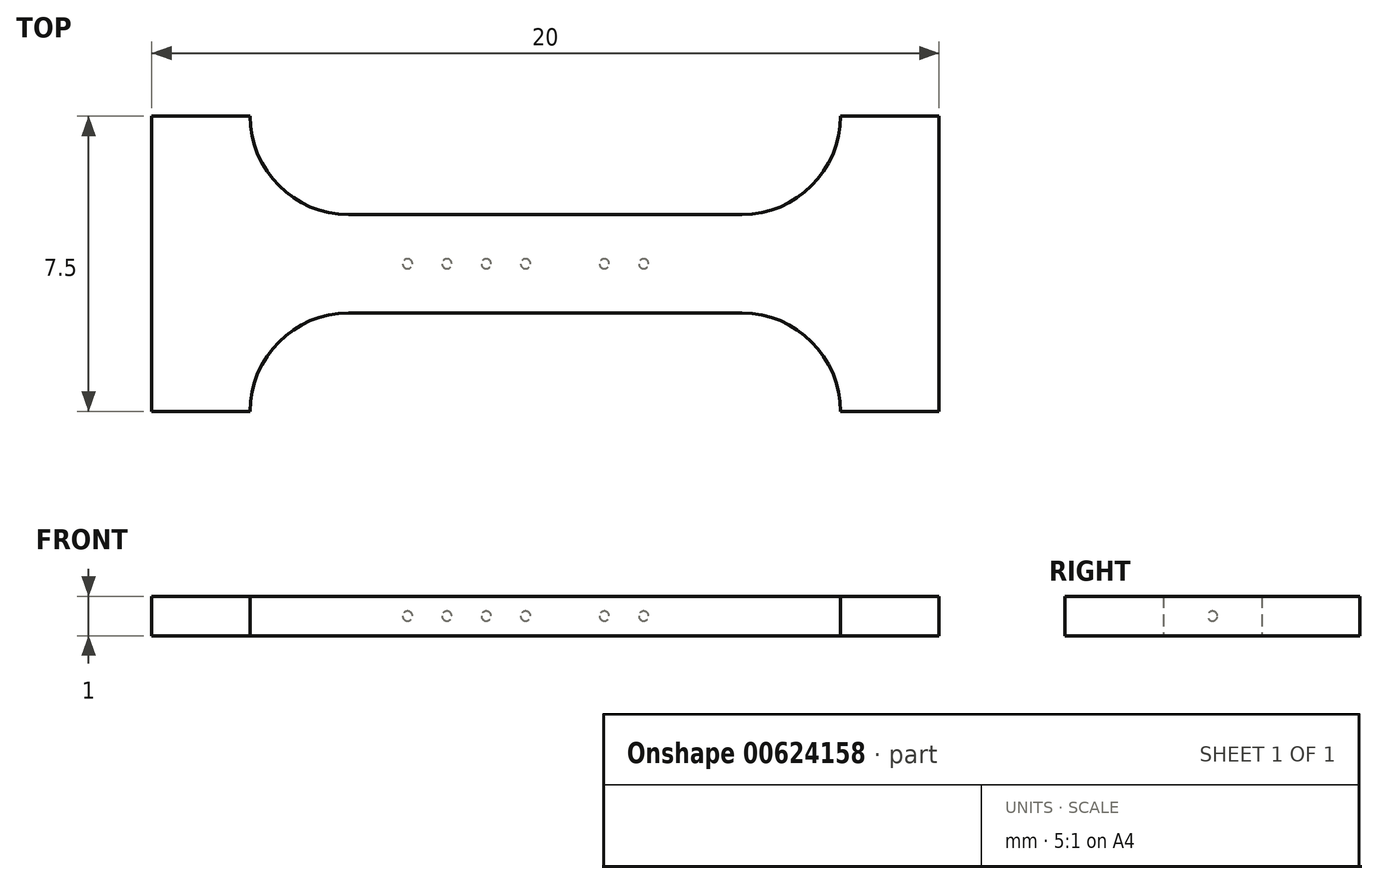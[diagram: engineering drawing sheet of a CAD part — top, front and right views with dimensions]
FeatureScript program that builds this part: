
annotation { "Feature Type Name" : "Feature", "Feature Type Description" : "" }
export const myFeature = defineFeature(function(context is Context, id is Id, definition is map)
    precondition{}
    {
        {
            var Q0;
            Q0=qCreatedBy(makeId("Top.planeOp"),FACE);
            var sketch = newSketch(context, id + "F0", { "sketchPlane" : qUnion([Q0])});
            skLineSegment(sketch, "E0.bottom", {"start": v(5, -1.25) * mm, "end": v(-5, -1.25) * mm, "construction": true});
            skLineSegment(sketch, "E0.top", {"start": v(5, 1.25) * mm, "end": v(-5, 1.25) * mm, "construction": true});
            skLineSegment(sketch, "E0.left", {"start": v(5, -1.25) * mm, "end": v(5, 1.25) * mm, "construction": true});
            skLineSegment(sketch, "E0.right", {"start": v(-5, -1.25) * mm, "end": v(-5, 1.25) * mm, "construction": true});
            skPoint(sketch, "E0.middle", {"position": v(0, 0) * mm});
            skLineSegment(sketch, "E1.bottom", {"start": v(5, 1.25) * mm, "end": v(7.5, 1.25) * mm, "construction": true});
            skLineSegment(sketch, "E1.top", {"start": v(5, -1.25) * mm, "end": v(7.5, -1.25) * mm, "construction": true});
            skLineSegment(sketch, "E1.left", {"start": v(5, 1.25) * mm, "end": v(5, -1.25) * mm, "construction": true});
            skLineSegment(sketch, "E1.right", {"start": v(7.5, 1.25) * mm, "end": v(7.5, -1.25) * mm, "construction": true});
            skLineSegment(sketch, "E2.bottom", {"start": v(7.5, 1.25) * mm, "end": v(10, 1.25) * mm, "construction": true});
            skLineSegment(sketch, "E2.top", {"start": v(7.5, -1.25) * mm, "end": v(10, -1.25) * mm, "construction": true});
            skLineSegment(sketch, "E2.right", {"start": v(10, 1.25) * mm, "end": v(10, -1.25) * mm, "construction": true});
            skLineSegment(sketch, "E3.top", {"start": v(7.5, 3.75) * mm, "end": v(10, 3.75) * mm, "construction": true});
            skLineSegment(sketch, "E3.left", {"start": v(7.5, 1.25) * mm, "end": v(7.5, 3.75) * mm, "construction": true});
            skLineSegment(sketch, "E3.right", {"start": v(10, 1.25) * mm, "end": v(10, 3.75) * mm, "construction": true});
            skLineSegment(sketch, "E4.top", {"start": v(7.5, -3.75) * mm, "end": v(10, -3.75) * mm, "construction": true});
            skLineSegment(sketch, "E4.left", {"start": v(7.5, -1.25) * mm, "end": v(7.5, -3.75) * mm, "construction": true});
            skLineSegment(sketch, "E4.right", {"start": v(10, -1.25) * mm, "end": v(10, -3.75) * mm, "construction": true});
            skLineSegment(sketch, "E5.bottom", {"start": v(7.5, 1.25) * mm, "end": v(5, 1.25) * mm, "construction": true});
            skLineSegment(sketch, "E5.top", {"start": v(7.5, 3.75) * mm, "end": v(5, 3.75) * mm, "construction": true});
            skLineSegment(sketch, "E5.right", {"start": v(5, 1.25) * mm, "end": v(5, 3.75) * mm, "construction": true});
            skArc(sketch, "E6", {"start": v(5, 1.25) * mm, "mid": v(6.77, 1.98) * mm, "end": v(7.5, 3.75) * mm});
            skLineSegment(sketch, "E7.top", {"start": v(5, -3.75) * mm, "end": v(7.5, -3.75) * mm, "construction": true});
            skLineSegment(sketch, "E7.left", {"start": v(5, -1.25) * mm, "end": v(5, -3.75) * mm, "construction": true});
            skArc(sketch, "E8", {"start": v(5, -1.25) * mm, "mid": v(6.77, -1.98) * mm, "end": v(7.5, -3.75) * mm});
            skLineSegment(sketch, "E9", {"start": v(7.5, -3.75) * mm, "end": v(10, -3.75) * mm});
            skLineSegment(sketch, "E10", {"start": v(10, -3.75) * mm, "end": v(10, 3.75) * mm});
            skLineSegment(sketch, "E11", {"start": v(10, 3.75) * mm, "end": v(7.5, 3.75) * mm});
            skLineSegment(sketch, "E12", {"start": v(0, 1.25) * mm, "end": v(0, -1.25) * mm, "construction": true});
            skLineSegment(sketch, "E13", {"start": v(5, 1.25) * mm, "end": v(0, 1.25) * mm});
            skLineSegment(sketch, "E14", {"start": v(0, 1.25) * mm, "end": v(0, -1.25) * mm});
            skLineSegment(sketch, "E15", {"start": v(0, -1.25) * mm, "end": v(5, -1.25) * mm});
            skLineSegment(sketch, "E16.bottom", {"start": v(-5, 1.25) * mm, "end": v(-7.5, 1.25) * mm, "construction": true});
            skLineSegment(sketch, "E16.top", {"start": v(-5, -1.25) * mm, "end": v(-7.5, -1.25) * mm, "construction": true});
            skLineSegment(sketch, "E16.left", {"start": v(-5, 1.25) * mm, "end": v(-5, -1.25) * mm, "construction": true});
            skLineSegment(sketch, "E16.right", {"start": v(-7.5, 1.25) * mm, "end": v(-7.5, -1.25) * mm, "construction": true});
            skLineSegment(sketch, "E17.bottom", {"start": v(-7.5, 1.25) * mm, "end": v(-10, 1.25) * mm, "construction": true});
            skLineSegment(sketch, "E17.top", {"start": v(-7.5, -1.25) * mm, "end": v(-10, -1.25) * mm, "construction": true});
            skLineSegment(sketch, "E17.right", {"start": v(-10, 1.25) * mm, "end": v(-10, -1.25) * mm, "construction": true});
            skLineSegment(sketch, "E18.bottom", {"start": v(-10, 1.25) * mm, "end": v(-7.5, 1.25) * mm, "construction": true});
            skLineSegment(sketch, "E18.top", {"start": v(-10, 3.75) * mm, "end": v(-7.5, 3.75) * mm, "construction": true});
            skLineSegment(sketch, "E18.left", {"start": v(-10, 1.25) * mm, "end": v(-10, 3.75) * mm, "construction": true});
            skLineSegment(sketch, "E18.right", {"start": v(-7.5, 1.25) * mm, "end": v(-7.5, 3.75) * mm, "construction": true});
            skLineSegment(sketch, "E19.bottom", {"start": v(-7.5, 3.75) * mm, "end": v(-5, 3.75) * mm, "construction": true});
            skLineSegment(sketch, "E19.top", {"start": v(-7.5, 1.25) * mm, "end": v(-5, 1.25) * mm, "construction": true});
            skLineSegment(sketch, "E19.left", {"start": v(-7.5, 3.75) * mm, "end": v(-7.5, 1.25) * mm, "construction": true});
            skLineSegment(sketch, "E19.right", {"start": v(-5, 3.75) * mm, "end": v(-5, 1.25) * mm, "construction": true});
            skLineSegment(sketch, "E20.bottom", {"start": v(-7.5, -1.25) * mm, "end": v(-5, -1.25) * mm, "construction": true});
            skLineSegment(sketch, "E20.top", {"start": v(-7.5, -3.75) * mm, "end": v(-5, -3.75) * mm, "construction": true});
            skLineSegment(sketch, "E20.left", {"start": v(-7.5, -1.25) * mm, "end": v(-7.5, -3.75) * mm, "construction": true});
            skLineSegment(sketch, "E20.right", {"start": v(-5, -1.25) * mm, "end": v(-5, -3.75) * mm, "construction": true});
            skLineSegment(sketch, "E21.bottom", {"start": v(-7.5, -3.75) * mm, "end": v(-10, -3.75) * mm, "construction": true});
            skLineSegment(sketch, "E21.left", {"start": v(-7.5, -3.75) * mm, "end": v(-7.5, -1.25) * mm, "construction": true});
            skLineSegment(sketch, "E21.right", {"start": v(-10, -3.75) * mm, "end": v(-10, -1.25) * mm, "construction": true});
            skArc(sketch, "E22", {"start": v(-7.5, 3.75) * mm, "mid": v(-6.77, 1.98) * mm, "end": v(-5, 1.25) * mm});
            skArc(sketch, "E23", {"start": v(-7.5, -3.75) * mm, "mid": v(-6.77, -1.98) * mm, "end": v(-5, -1.25) * mm});
            skLineSegment(sketch, "E24", {"start": v(-7.5, -3.75) * mm, "end": v(-10, -3.75) * mm});
            skLineSegment(sketch, "E25", {"start": v(-10, -3.75) * mm, "end": v(-10, 3.75) * mm});
            skLineSegment(sketch, "E26", {"start": v(-10, 3.75) * mm, "end": v(-7.5, 3.75) * mm});
            skLineSegment(sketch, "E27", {"start": v(-5, 1.25) * mm, "end": v(0, 1.25) * mm});
            skLineSegment(sketch, "E28", {"start": v(-5, -1.25) * mm, "end": v(0, -1.25) * mm});
            skSolve(sketch);
        }
        {
            var Q0;
            Q0=makeQuery(id+"F0.imprint","IMPRINT",FACE,{"disambiguationData":[TD([[makeQuery(id+"F0.imprint","IMPRINT",EDGE,{"derivedFrom":sQuery(id+"F0.wireOp",EDGE,"E14")}),-1.0]])]});
            var Q1;
            Q1=makeQuery(id+"F0.imprint","IMPRINT",FACE,{"disambiguationData":[TD([[makeQuery(id+"F0.imprint","IMPRINT",EDGE,{"derivedFrom":sQuery(id+"F0.wireOp",EDGE,"E6")}),-1.0]])]});
            extrude(context, id + "F1", {"entities" : qUnion([Q0, Q1]), "endBound" : BoundingType.SYMMETRIC, "depth" : 1 * mm, "offsetDistance" : 25 * mm});
        }
        {
            var Q0;
            Q0=qCreatedBy(makeId("Top.planeOp"),FACE);
            var sketch = newSketch(context, id + "F2", { "sketchPlane" : qUnion([Q0])});
            skLineSegment(sketch, "E29.bottom", {"start": v(5, -1.25) * mm, "end": v(-5, -1.25) * mm, "construction": true});
            skLineSegment(sketch, "E29.top", {"start": v(5, 1.25) * mm, "end": v(-5, 1.25) * mm, "construction": true});
            skLineSegment(sketch, "E29.left", {"start": v(5, -1.25) * mm, "end": v(5, 1.25) * mm, "construction": true});
            skLineSegment(sketch, "E29.right", {"start": v(-5, -1.25) * mm, "end": v(-5, 1.25) * mm, "construction": true});
            skPoint(sketch, "E29.middle", {"position": v(0, 0) * mm});
            skLineSegment(sketch, "E30.bottom", {"start": v(4.75, -1) * mm, "end": v(-4.75, -1) * mm, "construction": true});
            skLineSegment(sketch, "E30.top", {"start": v(4.75, 1) * mm, "end": v(-4.75, 1) * mm, "construction": true});
            skLineSegment(sketch, "E30.left", {"start": v(4.75, -1) * mm, "end": v(4.75, 1) * mm, "construction": true});
            skLineSegment(sketch, "E30.right", {"start": v(-4.75, -1) * mm, "end": v(-4.75, 1) * mm, "construction": true});
            skLineSegment(sketch, "E31", {"start": v(-4.75, 0) * mm, "end": v(4.75, 0) * mm});
            skCircle(sketch, "E32", {"center": v(-3.5, 0) * mm, "radius": 0.12 * mm});
            skCircle(sketch, "E33.1.0.0", {"center": v(-2.5, 0) * mm, "radius": 0.12 * mm});
            skCircle(sketch, "E33.2.0.0", {"center": v(-1.5, 0) * mm, "radius": 0.12 * mm});
            skCircle(sketch, "E33.3.0.0", {"center": v(-0.5, 0) * mm, "radius": 0.12 * mm});
            skCircle(sketch, "E33.4.0.0", {"center": v(0.5, 0) * mm, "radius": 0.12 * mm});
            skCircle(sketch, "E33.5.0.0", {"center": v(1.5, 0) * mm, "radius": 0.12 * mm});
            skCircle(sketch, "E33.6.0.0", {"center": v(2.5, 0) * mm, "radius": 0.12 * mm});
            skCircle(sketch, "E33.7.0.0", {"center": v(3.5, 0) * mm, "radius": 0.12 * mm});
            skLineSegment(sketch, "E33.direction1", {"start": v(-3.5, 0) * mm, "end": v(-2.5, 0) * mm, "construction": true});
            skSolve(sketch);
        }
        {
            var Q0;
            {var subQ0=sQuery(id+"F2.wireOp",EDGE,"E32");var subQ1=sQuery(id+"F2.wireOp",EDGE,"E31");var subQ2=makeQuery(id+"F2.imprint","INTERSECT",VERTEX,{"disambiguationData":[OD(0.0)],"derivedFrom":[subQ1,subQ0]});Q0=makeQuery(id+"F2.imprint","IMPRINT",FACE,{"disambiguationData":[TD([[makeQuery(id+"F2.imprint","IMPRINT",EDGE,{"disambiguationData":[TD([[subQ2,-1.0]])],"derivedFrom":subQ1}),-1.0]])]});}
            var Q1;
            {var subQ0=sQuery(id+"F2.wireOp",EDGE,"E33.1.0.0");var subQ1=sQuery(id+"F2.wireOp",EDGE,"E31");var subQ2=makeQuery(id+"F2.imprint","INTERSECT",VERTEX,{"disambiguationData":[OD(0.0)],"derivedFrom":[subQ1,subQ0]});Q1=makeQuery(id+"F2.imprint","IMPRINT",FACE,{"disambiguationData":[TD([[makeQuery(id+"F2.imprint","IMPRINT",EDGE,{"disambiguationData":[TD([[subQ2,-1.0]])],"derivedFrom":subQ1}),-1.0]])]});}
            var Q2;
            {var subQ0=sQuery(id+"F2.wireOp",EDGE,"E33.2.0.0");var subQ1=sQuery(id+"F2.wireOp",EDGE,"E31");var subQ2=makeQuery(id+"F2.imprint","INTERSECT",VERTEX,{"disambiguationData":[OD(0.0)],"derivedFrom":[subQ1,subQ0]});Q2=makeQuery(id+"F2.imprint","IMPRINT",FACE,{"disambiguationData":[TD([[makeQuery(id+"F2.imprint","IMPRINT",EDGE,{"disambiguationData":[TD([[subQ2,-1.0]])],"derivedFrom":subQ1}),-1.0]])]});}
            var Q3;
            {var subQ0=sQuery(id+"F2.wireOp",EDGE,"E33.3.0.0");var subQ1=sQuery(id+"F2.wireOp",EDGE,"E31");var subQ2=makeQuery(id+"F2.imprint","INTERSECT",VERTEX,{"disambiguationData":[OD(0.0)],"derivedFrom":[subQ1,subQ0]});Q3=makeQuery(id+"F2.imprint","IMPRINT",FACE,{"disambiguationData":[TD([[makeQuery(id+"F2.imprint","IMPRINT",EDGE,{"disambiguationData":[TD([[subQ2,-1.0]])],"derivedFrom":subQ1}),-1.0]])]});}
            var Q4;
            {var subQ0=sQuery(id+"F2.wireOp",EDGE,"E33.4.0.0");var subQ1=sQuery(id+"F2.wireOp",EDGE,"E31");var subQ2=makeQuery(id+"F2.imprint","INTERSECT",VERTEX,{"disambiguationData":[OD(0.0)],"derivedFrom":[subQ1,subQ0]});Q4=makeQuery(id+"F2.imprint","IMPRINT",FACE,{"disambiguationData":[TD([[makeQuery(id+"F2.imprint","IMPRINT",EDGE,{"disambiguationData":[TD([[subQ2,-1.0]])],"derivedFrom":subQ1}),-1.0]])]});}
            var Q5;
            {var subQ0=sQuery(id+"F2.wireOp",EDGE,"E33.5.0.0");var subQ1=sQuery(id+"F2.wireOp",EDGE,"E31");var subQ2=makeQuery(id+"F2.imprint","INTERSECT",VERTEX,{"disambiguationData":[OD(0.0)],"derivedFrom":[subQ1,subQ0]});Q5=makeQuery(id+"F2.imprint","IMPRINT",FACE,{"disambiguationData":[TD([[makeQuery(id+"F2.imprint","IMPRINT",EDGE,{"disambiguationData":[TD([[subQ2,-1.0]])],"derivedFrom":subQ1}),-1.0]])]});}
            var Q6;
            {var subQ0=sQuery(id+"F2.wireOp",EDGE,"E33.6.0.0");var subQ1=sQuery(id+"F2.wireOp",EDGE,"E31");var subQ2=makeQuery(id+"F2.imprint","INTERSECT",VERTEX,{"disambiguationData":[OD(0.0)],"derivedFrom":[subQ1,subQ0]});Q6=makeQuery(id+"F2.imprint","IMPRINT",FACE,{"disambiguationData":[TD([[makeQuery(id+"F2.imprint","IMPRINT",EDGE,{"disambiguationData":[TD([[subQ2,-1.0]])],"derivedFrom":subQ1}),-1.0]])]});}
            var Q7;
            {var subQ0=sQuery(id+"F2.wireOp",EDGE,"E33.7.0.0");var subQ1=sQuery(id+"F2.wireOp",EDGE,"E31");var subQ2=makeQuery(id+"F2.imprint","INTERSECT",VERTEX,{"disambiguationData":[OD(0.0)],"derivedFrom":[subQ1,subQ0]});Q7=makeQuery(id+"F2.imprint","IMPRINT",FACE,{"disambiguationData":[TD([[makeQuery(id+"F2.imprint","IMPRINT",EDGE,{"disambiguationData":[TD([[subQ2,-1.0]])],"derivedFrom":subQ1}),-1.0]])]});}
            var Q8;
            Q8=sQuery(id+"F2.wireOp",EDGE,"E31");
            revolve(context, id + "F3", {"operationType" : NewBodyOperationType.REMOVE, "entities" : qUnion([Q0, Q1, Q2, Q3, Q4, Q5, Q6, Q7]), "axis" : qUnion([Q8]), "revolveType" : RevolveType.FULL});
        }
        {
            var Q0;
            {var subQ0=sQuery(id+"F2.wireOp",EDGE,"E32");var subQ1=sQuery(id+"F2.wireOp",EDGE,"E31");var subQ2=makeQuery(id+"F2.imprint","INTERSECT",VERTEX,{"disambiguationData":[OD(0.0)],"derivedFrom":[subQ1,subQ0]});Q0=makeQuery(id+"F2.imprint","IMPRINT",FACE,{"disambiguationData":[TD([[makeQuery(id+"F2.imprint","IMPRINT",EDGE,{"disambiguationData":[TD([[subQ2,-1.0]])],"derivedFrom":subQ1}),-1.0]])]});}
            var Q1;
            {var subQ0=sQuery(id+"F2.wireOp",EDGE,"E33.1.0.0");var subQ1=sQuery(id+"F2.wireOp",EDGE,"E31");var subQ2=makeQuery(id+"F2.imprint","INTERSECT",VERTEX,{"disambiguationData":[OD(0.0)],"derivedFrom":[subQ1,subQ0]});Q1=makeQuery(id+"F2.imprint","IMPRINT",FACE,{"disambiguationData":[TD([[makeQuery(id+"F2.imprint","IMPRINT",EDGE,{"disambiguationData":[TD([[subQ2,-1.0]])],"derivedFrom":subQ1}),-1.0]])]});}
            var Q2;
            {var subQ0=sQuery(id+"F2.wireOp",EDGE,"E33.2.0.0");var subQ1=sQuery(id+"F2.wireOp",EDGE,"E31");var subQ2=makeQuery(id+"F2.imprint","INTERSECT",VERTEX,{"disambiguationData":[OD(0.0)],"derivedFrom":[subQ1,subQ0]});Q2=makeQuery(id+"F2.imprint","IMPRINT",FACE,{"disambiguationData":[TD([[makeQuery(id+"F2.imprint","IMPRINT",EDGE,{"disambiguationData":[TD([[subQ2,-1.0]])],"derivedFrom":subQ1}),-1.0]])]});}
            var Q3;
            {var subQ0=sQuery(id+"F2.wireOp",EDGE,"E33.3.0.0");var subQ1=sQuery(id+"F2.wireOp",EDGE,"E31");var subQ2=makeQuery(id+"F2.imprint","INTERSECT",VERTEX,{"disambiguationData":[OD(0.0)],"derivedFrom":[subQ1,subQ0]});Q3=makeQuery(id+"F2.imprint","IMPRINT",FACE,{"disambiguationData":[TD([[makeQuery(id+"F2.imprint","IMPRINT",EDGE,{"disambiguationData":[TD([[subQ2,-1.0]])],"derivedFrom":subQ1}),-1.0]])]});}
            var Q4;
            {var subQ0=sQuery(id+"F2.wireOp",EDGE,"E33.4.0.0");var subQ1=sQuery(id+"F2.wireOp",EDGE,"E31");var subQ2=makeQuery(id+"F2.imprint","INTERSECT",VERTEX,{"disambiguationData":[OD(0.0)],"derivedFrom":[subQ1,subQ0]});Q4=makeQuery(id+"F2.imprint","IMPRINT",FACE,{"disambiguationData":[TD([[makeQuery(id+"F2.imprint","IMPRINT",EDGE,{"disambiguationData":[TD([[subQ2,-1.0]])],"derivedFrom":subQ1}),-1.0]])]});}
            var Q5;
            {var subQ0=sQuery(id+"F2.wireOp",EDGE,"E33.5.0.0");var subQ1=sQuery(id+"F2.wireOp",EDGE,"E31");var subQ2=makeQuery(id+"F2.imprint","INTERSECT",VERTEX,{"disambiguationData":[OD(0.0)],"derivedFrom":[subQ1,subQ0]});Q5=makeQuery(id+"F2.imprint","IMPRINT",FACE,{"disambiguationData":[TD([[makeQuery(id+"F2.imprint","IMPRINT",EDGE,{"disambiguationData":[TD([[subQ2,-1.0]])],"derivedFrom":subQ1}),-1.0]])]});}
            var Q6;
            {var subQ0=sQuery(id+"F2.wireOp",EDGE,"E33.6.0.0");var subQ1=sQuery(id+"F2.wireOp",EDGE,"E31");var subQ2=makeQuery(id+"F2.imprint","INTERSECT",VERTEX,{"disambiguationData":[OD(0.0)],"derivedFrom":[subQ1,subQ0]});Q6=makeQuery(id+"F2.imprint","IMPRINT",FACE,{"disambiguationData":[TD([[makeQuery(id+"F2.imprint","IMPRINT",EDGE,{"disambiguationData":[TD([[subQ2,-1.0]])],"derivedFrom":subQ1}),-1.0]])]});}
            var Q7;
            {var subQ0=sQuery(id+"F2.wireOp",EDGE,"E33.7.0.0");var subQ1=sQuery(id+"F2.wireOp",EDGE,"E31");var subQ2=makeQuery(id+"F2.imprint","INTERSECT",VERTEX,{"disambiguationData":[OD(0.0)],"derivedFrom":[subQ1,subQ0]});Q7=makeQuery(id+"F2.imprint","IMPRINT",FACE,{"disambiguationData":[TD([[makeQuery(id+"F2.imprint","IMPRINT",EDGE,{"disambiguationData":[TD([[subQ2,-1.0]])],"derivedFrom":subQ1}),-1.0]])]});}
            var Q8;
            Q8=sQuery(id+"F2.wireOp",EDGE,"E31");
            revolve(context, id + "F4", {"entities" : qUnion([Q0, Q1, Q2, Q3, Q4, Q5, Q6, Q7]), "axis" : qUnion([Q8]), "revolveType" : RevolveType.FULL});
        }
    });
